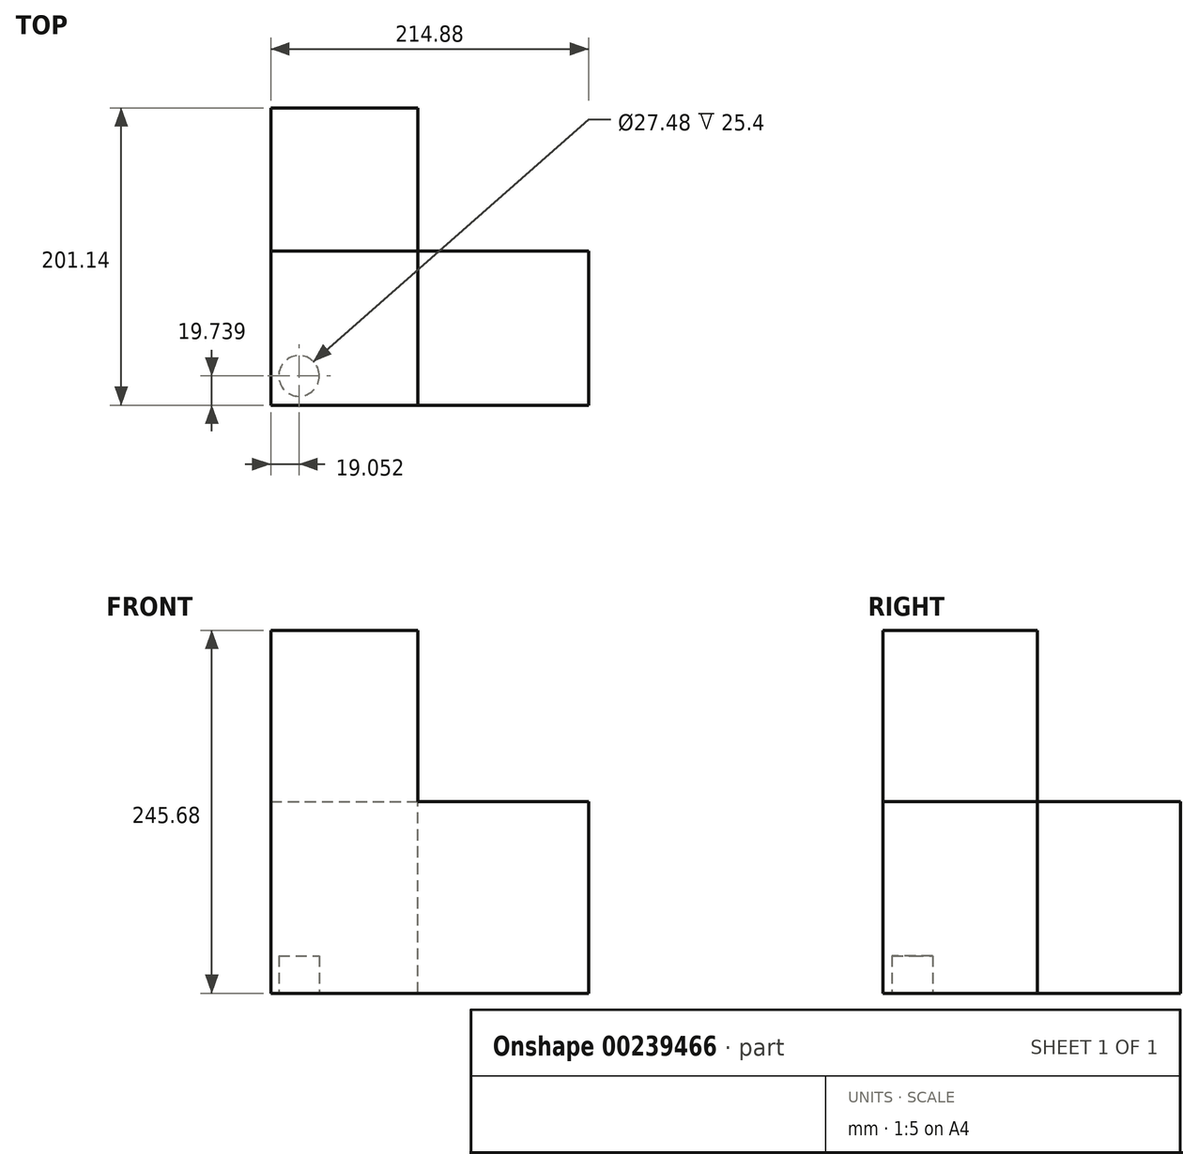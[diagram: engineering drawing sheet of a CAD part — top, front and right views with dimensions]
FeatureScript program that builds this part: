
annotation { "Feature Type Name" : "Feature", "Feature Type Description" : "" }
export const myFeature = defineFeature(function(context is Context, id is Id, definition is map)
    precondition{}
    {
        {
            var Q0;
            Q0=qCreatedBy(makeId("Right.planeOp"),FACE);
            var sketch = newSketch(context, id + "F0", { "sketchPlane" : qUnion([Q0])});
            skLineSegment(sketch, "E0.bottom", {"start": v(-52.18, 64.8) * mm, "end": v(52.18, 64.8) * mm});
            skLineSegment(sketch, "E0.top", {"start": v(-52.18, -64.8) * mm, "end": v(52.18, -64.8) * mm});
            skLineSegment(sketch, "E0.left", {"start": v(-52.18, 64.8) * mm, "end": v(-52.18, -64.8) * mm});
            skLineSegment(sketch, "E0.right", {"start": v(52.18, 64.8) * mm, "end": v(52.18, -64.8) * mm});
            skPoint(sketch, "E0.middle", {"position": v(0, 0) * mm});
            skSolve(sketch);
        }
        {
            var Q0;
            Q0 = qSketchRegion(id + "F0", true);
            extrude(context, id + "F1", {"entities" : qUnion([Q0]), "depth" : 214.88 * mm});
        }
        {
            var Q0;
            Q0=makeQuery(id+"F1.opExtrude","SWEPT_FACE",FACE,{"disambiguationData":[OSD([sQuery(id+"F0.wireOp",EDGE,"E0.bottom")])]});
            var sketch = newSketch(context, id + "F2", { "sketchPlane" : qUnion([Q0])});
            skLineSegment(sketch, "E1.bottom", {"start": v(0, -52.18) * mm, "end": v(99.35, -52.18) * mm});
            skLineSegment(sketch, "E1.top", {"start": v(0, 52.18) * mm, "end": v(99.35, 52.18) * mm});
            skLineSegment(sketch, "E1.left", {"start": v(0, -52.18) * mm, "end": v(0, 52.18) * mm});
            skLineSegment(sketch, "E1.right", {"start": v(99.35, -52.18) * mm, "end": v(99.35, 52.18) * mm});
            skSolve(sketch);
        }
        {
            var Q0;
            Q0 = qSketchRegion(id + "F2", true);
            extrude(context, id + "F3", {"entities" : qUnion([Q0]), "operationType" : NewBodyOperationType.ADD, "depth" : 116.08 * mm});
        }
        {
            var Q0;
            Q0=makeQuery(id+"F3.boolean.opBoolean","MERGE",FACE,{"derivedFrom":[makeQuery(id+"F1.opExtrude","SWEPT_FACE",FACE,{"disambiguationData":[OSD([sQuery(id+"F0.wireOp",EDGE,"E0.right")])]}),makeQuery(id+"F3.opExtrude","SWEPT_FACE",FACE,{"disambiguationData":[OSD([sQuery(id+"F2.wireOp",EDGE,"E1.top")])]})]});
            var sketch = newSketch(context, id + "F4", { "sketchPlane" : qUnion([Q0])});
            skLineSegment(sketch, "E2.bottom", {"start": v(0, -64.8) * mm, "end": v(-99.35, -64.8) * mm});
            skLineSegment(sketch, "E2.top", {"start": v(0, 64.8) * mm, "end": v(-99.35, 64.8) * mm});
            skLineSegment(sketch, "E2.left", {"start": v(0, -64.8) * mm, "end": v(0, 64.8) * mm});
            skLineSegment(sketch, "E2.right", {"start": v(-99.35, -64.8) * mm, "end": v(-99.35, 64.8) * mm});
            skSolve(sketch);
        }
        {
            var Q0;
            Q0 = qSketchRegion(id + "F4", true);
            extrude(context, id + "F5", {"entities" : qUnion([Q0]), "operationType" : NewBodyOperationType.ADD, "depth" : 96.77 * mm});
        }
        {
            var Q0;
            Q0=makeQuery(id+"F5.boolean.opBoolean","MERGE",FACE,{"derivedFrom":[makeQuery(id+"F1.opExtrude","SWEPT_FACE",FACE,{"disambiguationData":[OSD([sQuery(id+"F0.wireOp",EDGE,"E0.top")])]}),makeQuery(id+"F5.opExtrude","SWEPT_FACE",FACE,{"disambiguationData":[OSD([sQuery(id+"F4.wireOp",EDGE,"E2.bottom")])]})]});
            var sketch = newSketch(context, id + "F6", { "sketchPlane" : qUnion([Q0])});
            skCircle(sketch, "E3", {"center": v(19.05, 32.44) * mm, "radius": 13.74 * mm});
            skSolve(sketch);
        }
        {
            var Q0;
            Q0 = qSketchRegion(id + "F6", true);
            extrude(context, id + "F7", {"entities" : qUnion([Q0]), "operationType" : NewBodyOperationType.REMOVE, "oppositeDirection" : true, "depth" : 25.4 * mm});
        }
    });
